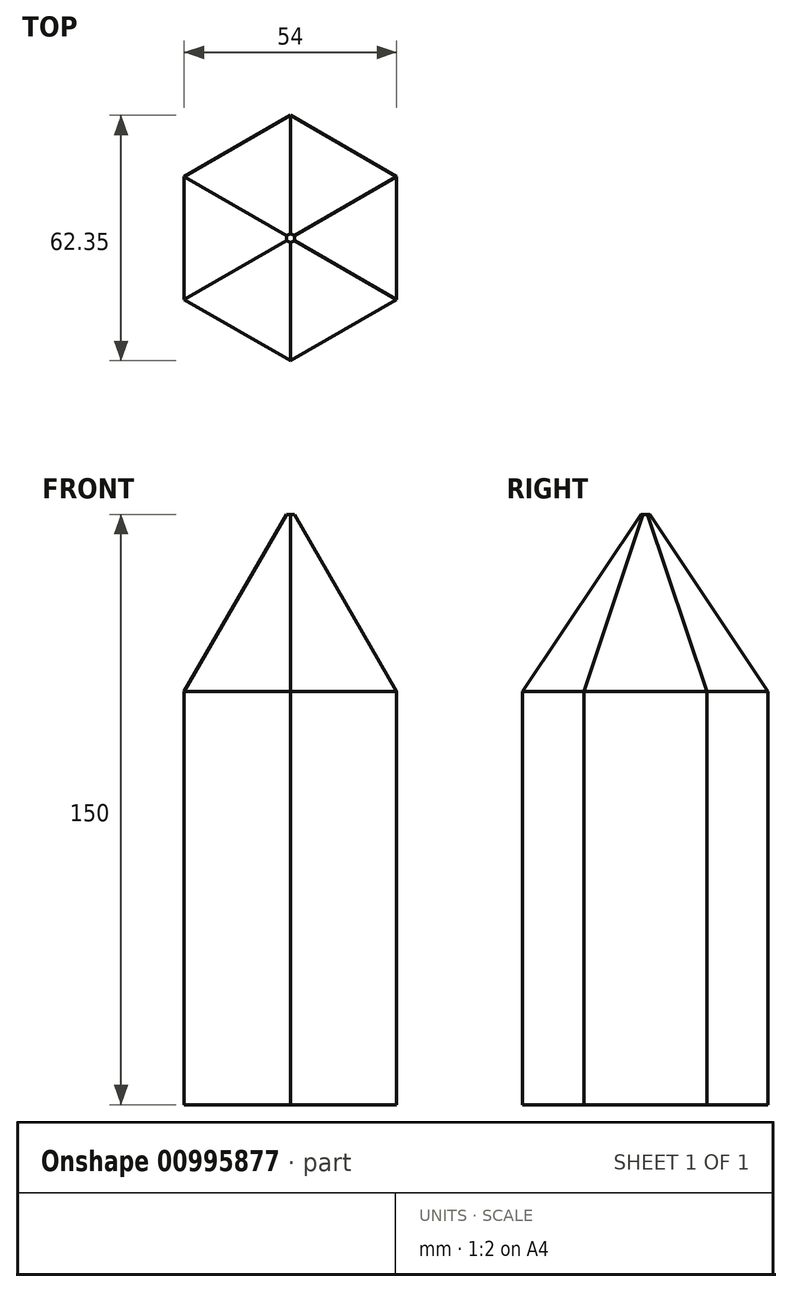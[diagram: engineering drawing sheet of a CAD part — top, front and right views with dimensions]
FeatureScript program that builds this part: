
annotation { "Feature Type Name" : "Feature", "Feature Type Description" : "" }
export const myFeature = defineFeature(function(context is Context, id is Id, definition is map)
    precondition{}
    {
        {
            var Q0;
            Q0=qCreatedBy(makeId("Top.planeOp"),FACE);
            var sketch = newSketch(context, id + "F0", { "sketchPlane" : qUnion([Q0])});
            skLineSegment(sketch, "E0", {"start": v(-24.4, 29.43) * mm, "end": v(2.6, 45.02) * mm});
            skLineSegment(sketch, "E1", {"start": v(2.6, 45.02) * mm, "end": v(29.6, 29.43) * mm});
            skLineSegment(sketch, "E2", {"start": v(29.6, 29.43) * mm, "end": v(29.6, -1.75) * mm});
            skLineSegment(sketch, "E3", {"start": v(29.6, -1.75) * mm, "end": v(2.6, -17.33) * mm});
            skLineSegment(sketch, "E4", {"start": v(2.6, -17.33) * mm, "end": v(-24.4, -1.75) * mm});
            skLineSegment(sketch, "E5", {"start": v(-24.4, -1.75) * mm, "end": v(-24.4, 29.43) * mm});
            skLineSegment(sketch, "E6", {"start": v(-24.4, 29.43) * mm, "end": v(29.6, 29.43) * mm});
            skLineSegment(sketch, "E7", {"start": v(2.6, 45.02) * mm, "end": v(29.6, -1.75) * mm});
            skLineSegment(sketch, "E8", {"start": v(2.6, 45.02) * mm, "end": v(-24.4, -1.75) * mm});
            skLineSegment(sketch, "E9", {"start": v(2.6, -17.33) * mm, "end": v(-24.4, 29.43) * mm});
            skLineSegment(sketch, "E10", {"start": v(29.6, 29.43) * mm, "end": v(2.6, -17.33) * mm});
            skLineSegment(sketch, "E11", {"start": v(29.6, -1.75) * mm, "end": v(-24.4, -1.75) * mm});
            skSolve(sketch);
        }
        {
            var Q0;
            Q0 = qSketchRegion(id + "F0", true);
            var Q1;
            {var subQ1=sQuery(id+"F0.wireOp",EDGE,"E8");var subQ5=sQuery(id+"F0.wireOp",EDGE,"E6");var subQ6=makeQuery(id+"F0.imprint","INTERSECT",VERTEX,{"derivedFrom":[subQ5,subQ1]});Q1=makeQuery(id+"F0.imprint","IMPRINT",FACE,{"disambiguationData":[TD([[makeQuery(id+"F0.imprint","IMPRINT",EDGE,{"disambiguationData":[TD([[subQ6,-1.0]])],"derivedFrom":subQ5}),-1.0]])]});}
            extrude(context, id + "F1", {"entities" : qUnion([Q0, Q1]), "depth" : 150 * mm, "offsetDistance" : 25 * mm});
        }
        {
            var Q0;
            Q0=makeQuery(id+"F1.opExtrude","CAP_FACE",FACE,{"disambiguationData":[OSD([sQuery(id+"F0.wireOp",EDGE,"E0"),sQuery(id+"F0.wireOp",EDGE,"E1"),sQuery(id+"F0.wireOp",EDGE,"E2"),sQuery(id+"F0.wireOp",EDGE,"E3"),sQuery(id+"F0.wireOp",EDGE,"E4"),sQuery(id+"F0.wireOp",EDGE,"E5")])],"isStart":false});
            chamfer(context, id + "F2", {"entities" : qUnion([Q0]), "chamferType" : ChamferType.OFFSET_ANGLE, "width" : 45 * mm, "oppositeDirection" : false, "angle" : 30 * degree});
        }
    });
